# Revit family: Grab_Bar-TSL-GR45RH-Arm_Support-THESPLASHLAB
name_source: partatom
category: Specialty Equipment
revit_build: Autodesk Revit 2016 (Build: 20160314_0715(x64)
units: mm (PartAtom-declared; Revit-internal decimal feet)

## family parameters
Cut with Voids When Loaded = No
Host = Face
OmniClass Number = 23.40.20.21.47
OmniClass Title = Bath Grab Bars
Part Type = Normal
Room Calculation Point = No
Round Connector Dimension = Use Diameter
Shared = No

## types (1)
- TSL-GR45RH_Satin
    Assembly Code = C1030200
    AssetType = fixed
    Default Elevation = 900 mm  [stored 2.95276 ft]
    Description = The TSL-GR45RH is a hinged single arm support bar. This grab bar has a locking mechanism which holds the bar in a vertical or horizontal position, and comes with concealed fixings and flush plate.
    DocumentationInstallationGuide = www.thesplashlab.com
    DocumentationLiterature = www.thesplashlab.com
    DocumentationMaintenance = www.thesplashlab.com
    DocumentationTechnical = www.thesplashlab.com
    DurationUnit = Years
    ExpectedLife = 2
    Finish = Satin
    Grade = 304
    Keynote = N13/340
    Manufacturer = The Splash Lab
    Manufacturer Tel = 0161 482 7000
    Material = Stainless Steel
    Model = TSL-GR45RH
    Mtrl_ExpectedLife = 0
    Mtrl_Finish = Satin
    Mtrl_Grade = 304
    Mtrl_Material = Stainless Steel
    Mtrl_ReplacementCost = 0
    Mtrl_SerialNumber = 0
    Mtrl_TagNumber = 0
    Mtrl_WarrantyDurationLabor = 0
    Mtrl_WarrantyDurationParts = 0
    Mtrl_bimspec_guid = 0
    Mtrl_current revision = 0
    NBSObjectName = Grab_Bar-TSL-GR45RH-Arm_Support-THESPLASHLAB
    NBSReference = 45-35-72/368
    Product Documentation Link = www.thesplashlab.com
    Product O&M Link = www.thesplashlab.com
    Product Page Link = www.thesplashlab.com
    Product Specification Link = www.thesplashlab.com
    Type Comments = Satin finish
    TypeName = TSL-GR45RH
    URL = www.thesplashlab.com
    Uniclass2 = 45-35-72/368
    WarrantyDescription = 2 years from date of purchase
    WarrantyDurationParts = 24
    WarrantyDurationUnit = months
    WarrantyStartDate = (default)
    _BIMspec_GUID = 0
    _current revision = 1
    _distributed by = www.thesplashlab.com
    finish = Steel-Splashlab-Satin
    material test = <By Category>

note: [stored X ft] marks values corroborated as IEEE doubles in the binary element streams (Revit-internal decimal feet)

## geometry (parser evidence)
native form markers: Blend x6, Sweep x8
no freeform markers — native parametric forms only
